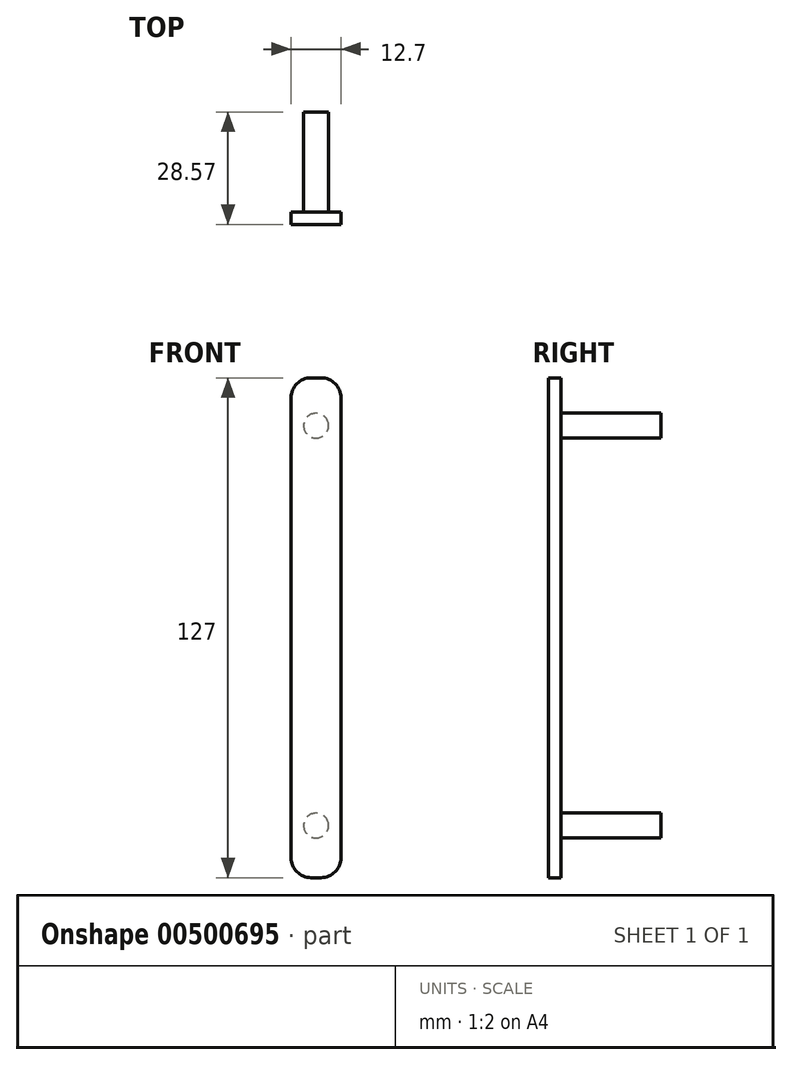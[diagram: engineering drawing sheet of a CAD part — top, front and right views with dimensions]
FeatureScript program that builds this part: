
annotation { "Feature Type Name" : "Feature", "Feature Type Description" : "" }
export const myFeature = defineFeature(function(context is Context, id is Id, definition is map)
    precondition{}
    {
        {
            var Q0;
            Q0=qCreatedBy(makeId("Front.planeOp"),FACE);
            var sketch = newSketch(context, id + "F0", { "sketchPlane" : qUnion([Q0])});
            skCircle(sketch, "E0", {"center": v(0, 0) * mm, "radius": 3.18 * mm});
            skCircle(sketch, "E1.0.1.0", {"center": v(0, 101.6) * mm, "radius": 3.18 * mm});
            skLineSegment(sketch, "E1.direction1", {"start": v(0, 0) * mm, "end": v(25.4, 0) * mm, "construction": true});
            skLineSegment(sketch, "E1.direction2", {"start": v(0, 0) * mm, "end": v(0, 101.6) * mm, "construction": true});
            skSolve(sketch);
        }
        {
            var Q0;
            Q0=makeQuery(id+"F0.imprint","IMPRINT",FACE,{"disambiguationData":[TD([[makeQuery(id+"F0.imprint","IMPRINT",EDGE,{"derivedFrom":sQuery(id+"F0.wireOp",EDGE,"E1.0.1.0")}),1.0]])]});
            var Q1;
            Q1=makeQuery(id+"F0.imprint","IMPRINT",FACE,{"disambiguationData":[TD([[makeQuery(id+"F0.imprint","IMPRINT",EDGE,{"derivedFrom":sQuery(id+"F0.wireOp",EDGE,"E0")}),1.0]])]});
            extrude(context, id + "F1", {"entities" : qUnion([Q0, Q1]), "depth" : 25.4 * mm, "offsetDistance" : 25.4 * mm});
        }
        {
            var Q0;
            Q0=makeQuery(id+"F1.opExtrude","CAP_FACE",FACE,{"disambiguationData":[OSD([sQuery(id+"F0.wireOp",EDGE,"E1.0.1.0")])],"isStart":false});
            var sketch = newSketch(context, id + "F2", { "sketchPlane" : qUnion([Q0])});
            skLineSegment(sketch, "E2.bottom", {"start": v(0, -13.23) * mm, "end": v(6.35, -13.23) * mm});
            skLineSegment(sketch, "E2.top", {"start": v(0, 113.77) * mm, "end": v(6.35, 113.77) * mm});
            skLineSegment(sketch, "E2.left", {"start": v(0, -13.23) * mm, "end": v(0, 113.77) * mm, "construction": true});
            skLineSegment(sketch, "E2.right", {"start": v(6.35, -13.23) * mm, "end": v(6.35, 113.77) * mm});
            skLineSegment(sketch, "E3.MirrorCS", {"start": v(0, 113.77) * mm, "end": v(-6.35, 113.77) * mm});
            skLineSegment(sketch, "E4.MirrorCS", {"start": v(-6.35, -13.23) * mm, "end": v(-6.35, 113.77) * mm});
            skLineSegment(sketch, "E5.MirrorCS", {"start": v(0, -13.23) * mm, "end": v(-6.35, -13.23) * mm});
            skSolve(sketch);
        }
        {
            var Q0;
            Q0 = qSketchRegion(id + "F2", true);
            extrude(context, id + "F3", {"entities" : qUnion([Q0]), "operationType" : NewBodyOperationType.ADD, "depth" : 3.17 * mm, "offsetDistance" : 25.4 * mm});
        }
        {
            var Q0;
            Q0=makeQuery(id+"F3.opExtrude","SWEPT_EDGE",EDGE,{"disambiguationData":[OSD([sQuery(id+"F2.wireOp",EDGE,"E3.MirrorCS"),sQuery(id+"F2.wireOp",EDGE,"E4.MirrorCS")])]});
            var Q1;
            Q1=makeQuery(id+"F3.opExtrude","SWEPT_EDGE",EDGE,{"disambiguationData":[OSD([sQuery(id+"F2.wireOp",EDGE,"E2.top"),sQuery(id+"F2.wireOp",EDGE,"E2.right")])]});
            var Q2;
            Q2=makeQuery(id+"F3.opExtrude","SWEPT_EDGE",EDGE,{"disambiguationData":[OSD([sQuery(id+"F2.wireOp",EDGE,"E2.bottom"),sQuery(id+"F2.wireOp",EDGE,"E2.right")])]});
            var Q3;
            Q3=makeQuery(id+"F3.opExtrude","SWEPT_EDGE",EDGE,{"disambiguationData":[OSD([sQuery(id+"F2.wireOp",EDGE,"E4.MirrorCS"),sQuery(id+"F2.wireOp",EDGE,"E5.MirrorCS")])]});
            fillet(context, id + "F4", {"entities" : qUnion([Q0, Q1, Q2, Q3]), "radius" : 5.08 * mm, "tangentPropagation" : true, "allowEdgeOverflow" : false});
        }
    });
